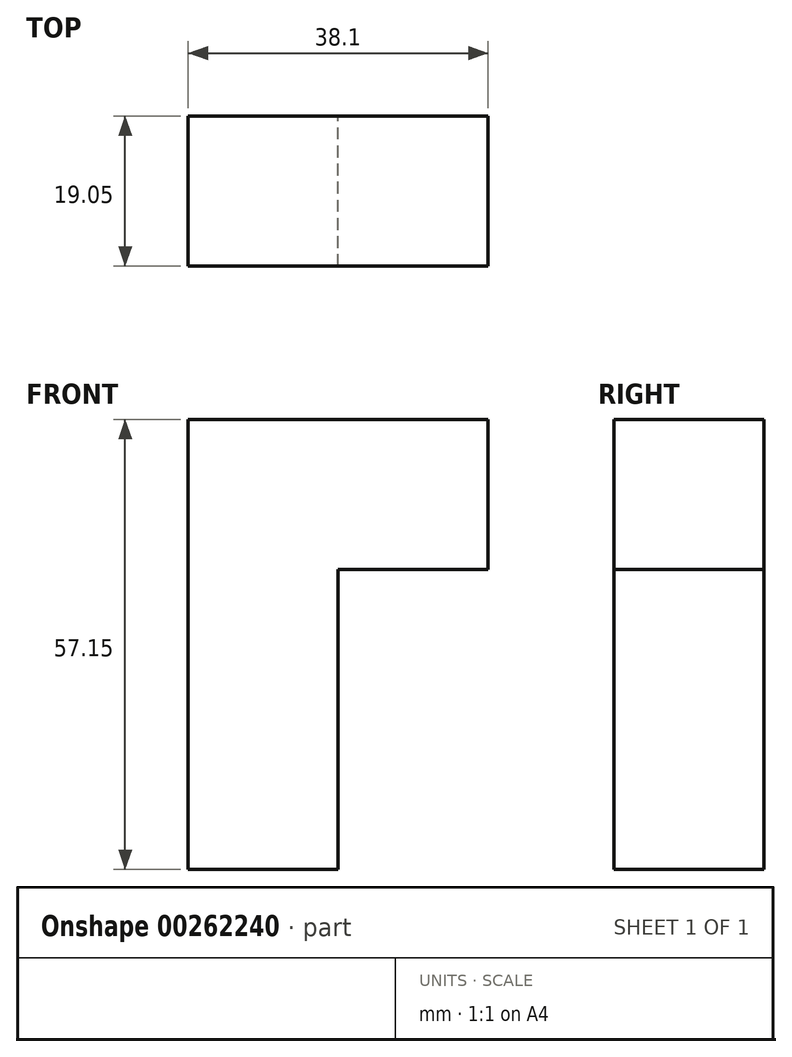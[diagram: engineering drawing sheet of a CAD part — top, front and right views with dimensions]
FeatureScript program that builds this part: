
annotation { "Feature Type Name" : "Feature", "Feature Type Description" : "" }
export const myFeature = defineFeature(function(context is Context, id is Id, definition is map)
    precondition{}
    {
        {
            var Q0;
            Q0=qCreatedBy(makeId("Front.planeOp"),FACE);
            var sketch = newSketch(context, id + "F0", { "sketchPlane" : qUnion([Q0])});
            skLineSegment(sketch, "E0.bottom", {"start": v(-64.43, 44.08) * mm, "end": v(-45.38, 44.08) * mm});
            skLineSegment(sketch, "E0.top", {"start": v(-64.43, 25.03) * mm, "end": v(-45.38, 25.03) * mm});
            skLineSegment(sketch, "E0.left", {"start": v(-64.43, 44.08) * mm, "end": v(-64.43, 25.03) * mm});
            skLineSegment(sketch, "E0.right", {"start": v(-45.38, 44.08) * mm, "end": v(-45.38, 25.03) * mm});
            skLineSegment(sketch, "E1", {"start": v(-64.43, 25.03) * mm, "end": v(-64.43, 5.98) * mm});
            skLineSegment(sketch, "E2", {"start": v(-64.43, 5.98) * mm, "end": v(-64.43, -13.07) * mm});
            skLineSegment(sketch, "E3", {"start": v(-45.38, 25.03) * mm, "end": v(-45.38, 5.98) * mm});
            skLineSegment(sketch, "E4", {"start": v(-45.38, 5.98) * mm, "end": v(-45.38, -13.07) * mm});
            skLineSegment(sketch, "E5", {"start": v(-64.43, -13.07) * mm, "end": v(-45.38, -13.07) * mm});
            skLineSegment(sketch, "E6", {"start": v(-45.38, 5.98) * mm, "end": v(-64.43, 5.98) * mm});
            skLineSegment(sketch, "E7", {"start": v(-45.38, 44.08) * mm, "end": v(-26.33, 44.08) * mm});
            skLineSegment(sketch, "E8", {"start": v(-45.38, 25.03) * mm, "end": v(-26.33, 25.03) * mm});
            skLineSegment(sketch, "E9", {"start": v(-26.33, 44.08) * mm, "end": v(-26.33, 25.03) * mm});
            skSolve(sketch);
        }
        {
            var Q0;
            Q0=makeQuery(id+"F0.imprint","IMPRINT",FACE,{"disambiguationData":[TD([[makeQuery(id+"F0.imprint","IMPRINT",EDGE,{"derivedFrom":sQuery(id+"F0.wireOp",EDGE,"E0.bottom")}),-1.0]])]});
            var Q1;
            Q1=makeQuery(id+"F0.imprint","IMPRINT",FACE,{"disambiguationData":[TD([[makeQuery(id+"F0.imprint","IMPRINT",EDGE,{"derivedFrom":sQuery(id+"F0.wireOp",EDGE,"E0.right")}),1.0]])]});
            var Q2;
            Q2=makeQuery(id+"F0.imprint","IMPRINT",FACE,{"disambiguationData":[TD([[makeQuery(id+"F0.imprint","IMPRINT",EDGE,{"derivedFrom":sQuery(id+"F0.wireOp",EDGE,"E0.top")}),-1.0]])]});
            var Q3;
            Q3=makeQuery(id+"F0.imprint","IMPRINT",FACE,{"disambiguationData":[TD([[makeQuery(id+"F0.imprint","IMPRINT",EDGE,{"derivedFrom":sQuery(id+"F0.wireOp",EDGE,"E2")}),1.0]])]});
            extrude(context, id + "F1", {"entities" : qUnion([Q0, Q1, Q2, Q3]), "depth" : 19.05 * mm});
        }
    });
